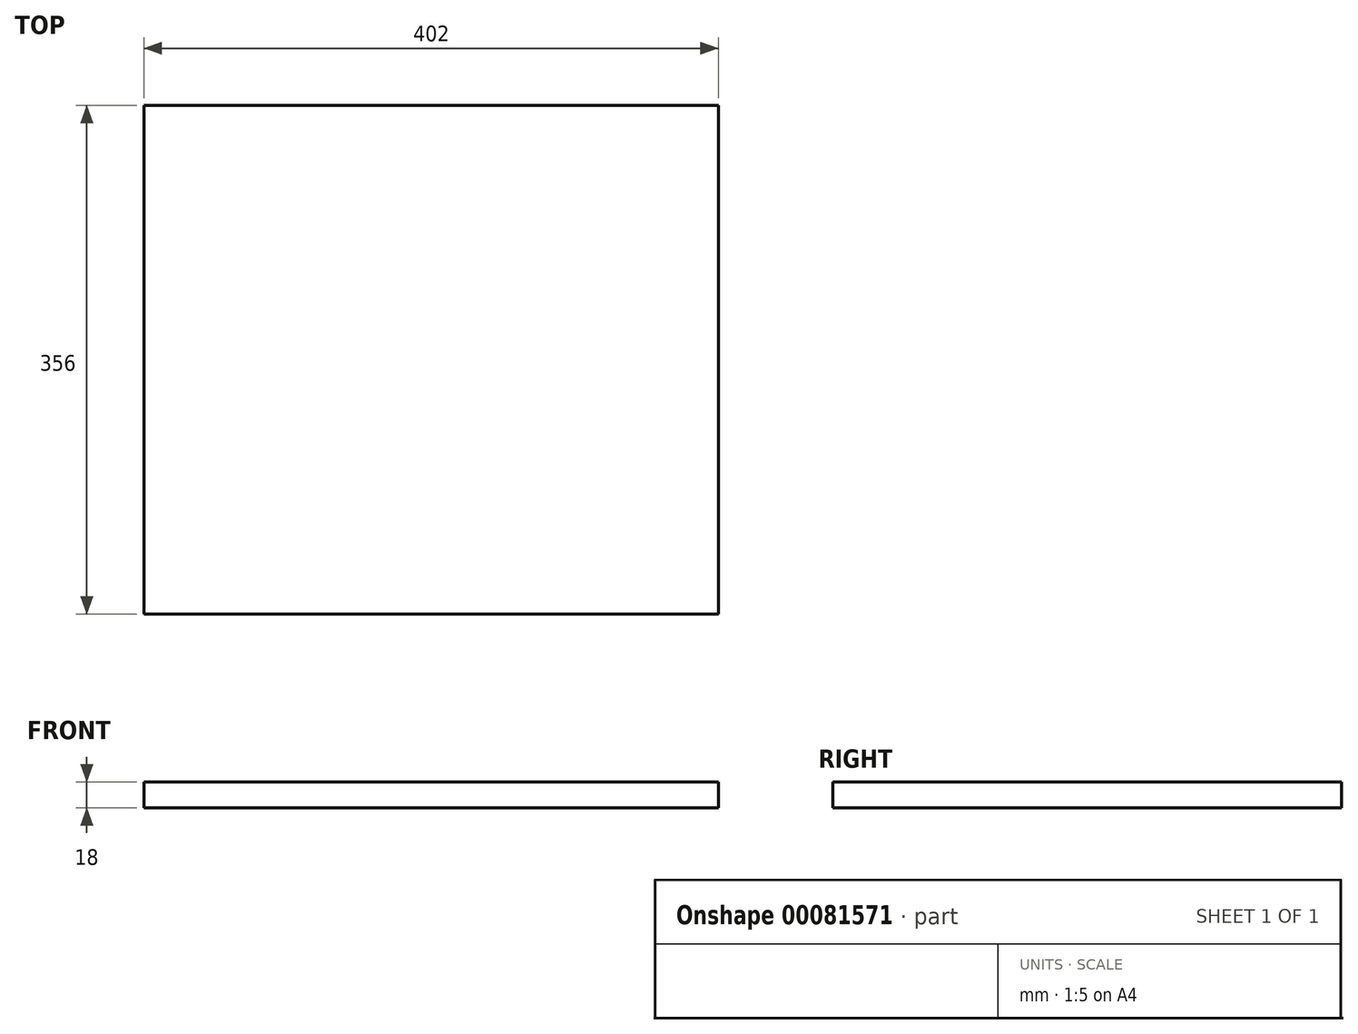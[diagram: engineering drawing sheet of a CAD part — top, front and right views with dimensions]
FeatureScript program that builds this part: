
annotation { "Feature Type Name" : "Feature", "Feature Type Description" : "" }
export const myFeature = defineFeature(function(context is Context, id is Id, definition is map)
    precondition{}
    {
        {
            var Q0;
            Q0=qCreatedBy(makeId("Top.planeOp"),FACE);
            var sketch = newSketch(context, id + "F0", { "sketchPlane" : qUnion([Q0])});
            skLineSegment(sketch, "E0.bottom", {"start": v(0, 0) * mm, "end": v(402, 0) * mm});
            skLineSegment(sketch, "E0.top", {"start": v(0, 356) * mm, "end": v(402, 356) * mm});
            skLineSegment(sketch, "E0.left", {"start": v(0, 0) * mm, "end": v(0, 356) * mm});
            skLineSegment(sketch, "E0.right", {"start": v(402, 0) * mm, "end": v(402, 356) * mm});
            skSolve(sketch);
        }
        {
            var Q0;
            Q0 = qSketchRegion(id + "F0", true);
            extrude(context, id + "F1", {"entities" : qUnion([Q0]), "depth" : 18 * mm});
        }
    });
